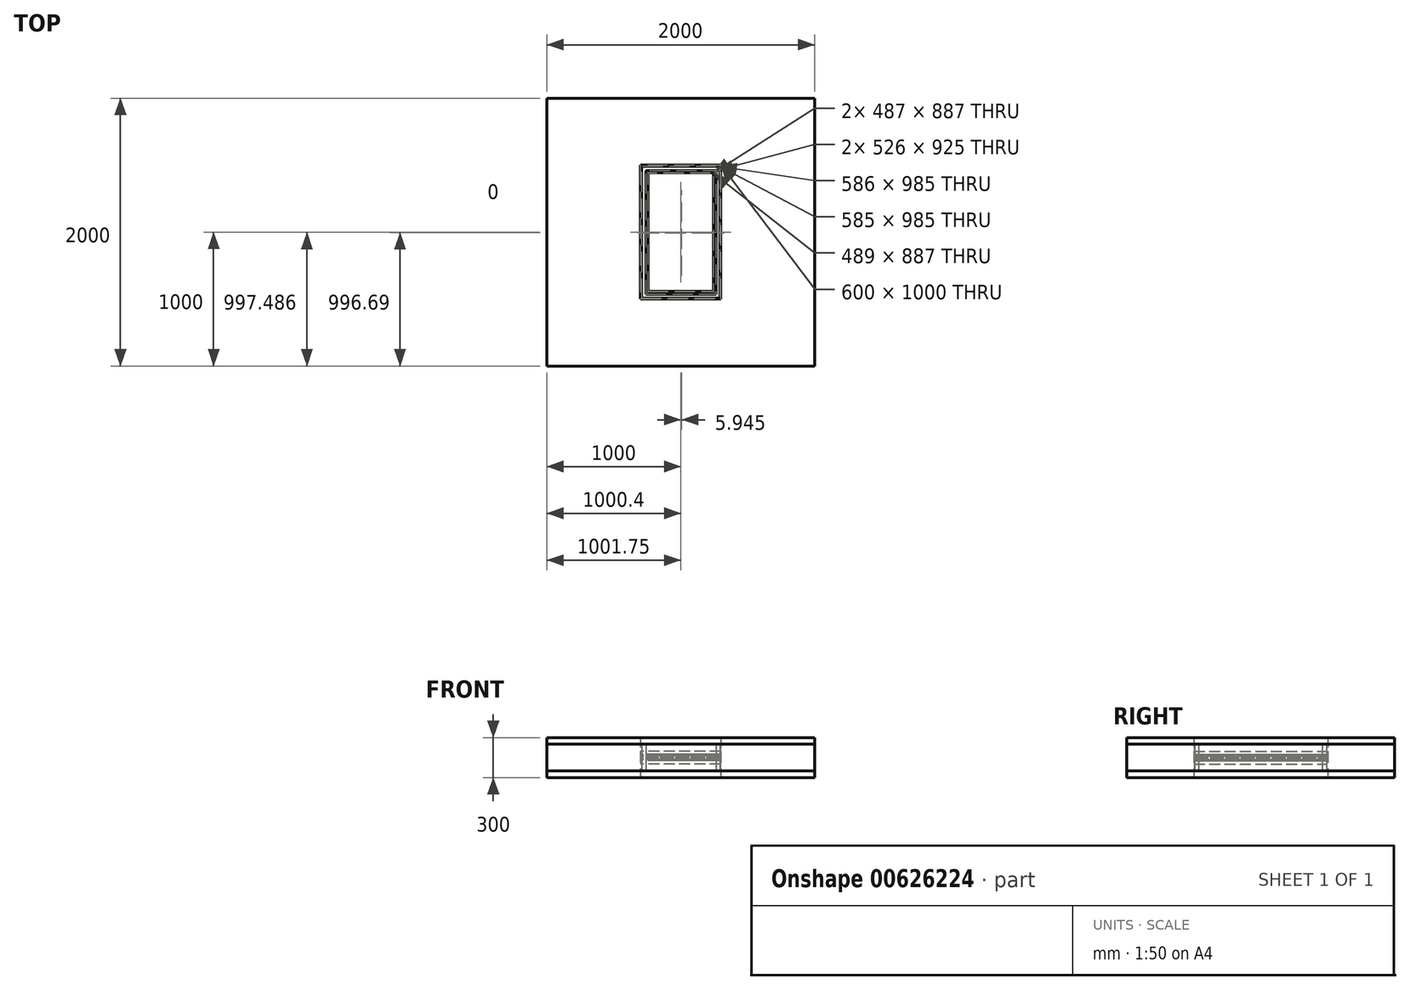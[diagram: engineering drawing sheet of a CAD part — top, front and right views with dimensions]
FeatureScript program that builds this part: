
annotation { "Feature Type Name" : "Feature", "Feature Type Description" : "" }
export const myFeature = defineFeature(function(context is Context, id is Id, definition is map)
    precondition{}
    {
        {
            var Q0;
            Q0=qCreatedBy(makeId("Top.planeOp"),FACE);
            var sketch = newSketch(context, id + "F0", { "sketchPlane" : qUnion([Q0])});
            skLineSegment(sketch, "E0.bottom", {"start": v(300, -500) * mm, "end": v(-300, -500) * mm});
            skLineSegment(sketch, "E0.top", {"start": v(300, 500) * mm, "end": v(-300, 500) * mm});
            skLineSegment(sketch, "E0.left", {"start": v(300, -500) * mm, "end": v(300, 500) * mm});
            skLineSegment(sketch, "E0.right", {"start": v(-300, -500) * mm, "end": v(-300, 500) * mm});
            skPoint(sketch, "E0.middle", {"position": v(0, 0) * mm});
            skLineSegment(sketch, "E1.0", {"start": v(-292.5, -492.5) * mm, "end": v(-292.5, 492.5) * mm});
            skLineSegment(sketch, "E1.1", {"start": v(292.5, -492.5) * mm, "end": v(-292.5, -492.5) * mm});
            skLineSegment(sketch, "E1.2", {"start": v(292.5, -492.5) * mm, "end": v(292.5, 492.5) * mm});
            skLineSegment(sketch, "E1.3", {"start": v(292.5, 492.5) * mm, "end": v(-292.5, 492.5) * mm});
            skSolve(sketch);
        }
        {
            var Q0;
            Q0 = qSketchRegion(id + "F0", true);
            extrude(context, id + "F1", {"entities" : qUnion([Q0]), "endBound" : BoundingType.SYMMETRIC, "depth" : 96 * mm, "offsetDistance" : 25 * mm});
        }
        {
            var Q0;
            Q0=qCreatedBy(makeId("Top.planeOp"),FACE);
            var sketch = newSketch(context, id + "F2", { "sketchPlane" : qUnion([Q0])});
            skPoint(sketch, "E2.middle", {"position": v(0, 0) * mm});
            skLineSegment(sketch, "E3.0", {"start": v(-292.5, -492.5) * mm, "end": v(-292.5, 492.5) * mm});
            skLineSegment(sketch, "E3.1", {"start": v(292.5, -492.5) * mm, "end": v(-292.5, -492.5) * mm});
            skLineSegment(sketch, "E3.2", {"start": v(292.5, -492.5) * mm, "end": v(292.5, 492.5) * mm});
            skLineSegment(sketch, "E3.3", {"start": v(292.5, 492.5) * mm, "end": v(-292.5, 492.5) * mm});
            skLineSegment(sketch, "E4.0", {"start": v(243.5, -443.5) * mm, "end": v(243.5, 443.5) * mm});
            skLineSegment(sketch, "E4.1", {"start": v(243.5, -443.5) * mm, "end": v(-243.5, -443.5) * mm});
            skLineSegment(sketch, "E4.2", {"start": v(-243.5, -443.5) * mm, "end": v(-243.5, 443.5) * mm});
            skLineSegment(sketch, "E4.3", {"start": v(243.5, 443.5) * mm, "end": v(-243.5, 443.5) * mm});
            skSolve(sketch);
        }
        {
            var Q0;
            Q0=makeQuery(id+"F2.imprint","IMPRINT",FACE,{"disambiguationData":[TD([[makeQuery(id+"F2.imprint","IMPRINT",EDGE,{"derivedFrom":sQuery(id+"F2.wireOp",EDGE,"E3.0")}),-1.0]])]});
            extrude(context, id + "F3", {"entities" : qUnion([Q0]), "endBound" : BoundingType.SYMMETRIC, "depth" : 48 * mm, "offsetDistance" : 25 * mm});
        }
        {
            var Q0;
            Q0=qCreatedBy(makeId("Top.planeOp"),FACE);
            var sketch = newSketch(context, id + "F4", { "sketchPlane" : qUnion([Q0])});
            skPoint(sketch, "E5.middle", {"position": v(5.95, -5.93) * mm});
            skLineSegment(sketch, "E6.0", {"start": v(-286.55, -498.43) * mm, "end": v(-286.55, 486.57) * mm});
            skLineSegment(sketch, "E6.1", {"start": v(298.45, -498.43) * mm, "end": v(-286.55, -498.43) * mm});
            skLineSegment(sketch, "E6.2", {"start": v(298.45, -498.43) * mm, "end": v(298.45, 486.57) * mm});
            skLineSegment(sketch, "E6.3", {"start": v(298.45, 486.57) * mm, "end": v(-286.55, 486.57) * mm});
            skLineSegment(sketch, "E7.0", {"start": v(249.45, -449.43) * mm, "end": v(249.45, 437.57) * mm});
            skLineSegment(sketch, "E7.1", {"start": v(249.45, -449.43) * mm, "end": v(-237.55, -449.43) * mm});
            skLineSegment(sketch, "E7.2", {"start": v(-237.55, -449.43) * mm, "end": v(-237.55, 437.57) * mm});
            skLineSegment(sketch, "E7.3", {"start": v(249.45, 437.57) * mm, "end": v(-237.55, 437.57) * mm});
            skSolve(sketch);
        }
        {
            var Q0;
            Q0=makeQuery(id+"F4.imprint","IMPRINT",FACE,{"disambiguationData":[TD([[makeQuery(id+"F4.imprint","IMPRINT",EDGE,{"derivedFrom":sQuery(id+"F4.wireOp",EDGE,"E6.0")}),-1.0]])]});
            extrude(context, id + "F5", {"entities" : qUnion([Q0]), "endBound" : BoundingType.SYMMETRIC, "depth" : 24 * mm, "offsetDistance" : 25 * mm});
        }
        {
            var Q0;
            Q0=qCreatedBy(makeId("Top.planeOp"),FACE);
            var sketch = newSketch(context, id + "F6", { "sketchPlane" : qUnion([Q0])});
            skLineSegment(sketch, "E8.0", {"start": v(-291.25, -495.01) * mm, "end": v(-291.25, 489.99) * mm});
            skLineSegment(sketch, "E8.1", {"start": v(294.75, -495.01) * mm, "end": v(-291.25, -495.01) * mm});
            skLineSegment(sketch, "E8.2", {"start": v(294.75, -495.01) * mm, "end": v(294.75, 489.99) * mm});
            skLineSegment(sketch, "E8.3", {"start": v(294.75, 489.99) * mm, "end": v(-291.25, 489.99) * mm});
            skLineSegment(sketch, "E9.0", {"start": v(264.75, 459.99) * mm, "end": v(-261.25, 459.99) * mm});
            skLineSegment(sketch, "E9.1", {"start": v(264.75, -465.01) * mm, "end": v(264.75, 459.99) * mm});
            skLineSegment(sketch, "E9.2", {"start": v(264.75, -465.01) * mm, "end": v(-261.25, -465.01) * mm});
            skLineSegment(sketch, "E9.3", {"start": v(-261.25, -465.01) * mm, "end": v(-261.25, 459.99) * mm});
            skSolve(sketch);
        }
        {
            var Q0;
            Q0=makeQuery(id+"F6.imprint","IMPRINT",FACE,{"disambiguationData":[TD([[makeQuery(id+"F6.imprint","IMPRINT",EDGE,{"derivedFrom":sQuery(id+"F6.wireOp",EDGE,"E9.0")}),1.0]])]});
            extrude(context, id + "F7", {"entities" : qUnion([Q0]), "depth" : 25 * mm, "offsetDistance" : 25 * mm});
        }
        {
            var Q0;
            Q0=makeQuery(id+"F7.opExtrude","SWEPT_BODY",BODY,{"disambiguationData":[OSD([sQuery(id+"F6.wireOp",EDGE,"E9.0"),sQuery(id+"F6.wireOp",EDGE,"E9.1"),sQuery(id+"F6.wireOp",EDGE,"E9.2"),sQuery(id+"F6.wireOp",EDGE,"E9.3")])]});
            deleteBodies(context, id + "F8", {"entities" : qUnion([Q0])});
        }
        {
            var Q0;
            Q0=makeQuery(id+"F6.imprint","IMPRINT",FACE,{"disambiguationData":[TD([[makeQuery(id+"F6.imprint","IMPRINT",EDGE,{"derivedFrom":sQuery(id+"F6.wireOp",EDGE,"E8.0")}),-1.0]])]});
            extrude(context, id + "F9", {"entities" : qUnion([Q0]), "depth" : 24 * mm, "offsetDistance" : 25 * mm});
        }
        {
            var Q0;
            Q0=makeQuery(id+"F6.imprint","IMPRINT",FACE,{"disambiguationData":[TD([[makeQuery(id+"F6.imprint","IMPRINT",EDGE,{"derivedFrom":sQuery(id+"F6.wireOp",EDGE,"E9.0")}),1.0]])]});
            var sketch = newSketch(context, id + "F10", { "sketchPlane" : qUnion([Q0])});
            skLineSegment(sketch, "E10.0", {"start": v(263.9, 459.2) * mm, "end": v(-263.1, 459.2) * mm});
            skLineSegment(sketch, "E10.1", {"start": v(263.9, -465.8) * mm, "end": v(263.9, 459.2) * mm});
            skLineSegment(sketch, "E10.2", {"start": v(263.9, -465.8) * mm, "end": v(-263.1, -465.8) * mm});
            skLineSegment(sketch, "E10.3", {"start": v(-263.1, -465.8) * mm, "end": v(-263.1, 459.2) * mm});
            skLineSegment(sketch, "E11.0", {"start": v(-244.1, -446.8) * mm, "end": v(-244.1, 440.2) * mm});
            skLineSegment(sketch, "E11.1", {"start": v(244.9, -446.8) * mm, "end": v(-244.1, -446.8) * mm});
            skLineSegment(sketch, "E11.2", {"start": v(244.9, -446.8) * mm, "end": v(244.9, 440.2) * mm});
            skLineSegment(sketch, "E11.3", {"start": v(244.9, 440.2) * mm, "end": v(-244.1, 440.2) * mm});
            skSolve(sketch);
        }
        {
            var Q0;
            Q0=makeQuery(id+"F10.imprint","IMPRINT",FACE,{"disambiguationData":[TD([[makeQuery(id+"F10.imprint","IMPRINT",EDGE,{"derivedFrom":sQuery(id+"F10.wireOp",EDGE,"E11.0")}),1.0]])]});
            extrude(context, id + "F11", {"entities" : qUnion([Q0]), "endBound" : BoundingType.SYMMETRIC, "depth" : 24 * mm, "offsetDistance" : 25 * mm});
        }
        {
            var Q0;
            Q0=makeQuery(id+"F6.imprint","IMPRINT",FACE,{"disambiguationData":[TD([[makeQuery(id+"F6.imprint","IMPRINT",EDGE,{"derivedFrom":sQuery(id+"F6.wireOp",EDGE,"E8.0")}),-1.0]])]});
            extrude(context, id + "F12", {"entities" : qUnion([Q0]), "endBound" : BoundingType.SYMMETRIC, "depth" : 200 * mm, "offsetDistance" : 25 * mm});
        }
        {
            var Q0;
            Q0=qCreatedBy(makeId("Top.planeOp"),FACE);
            var sketch = newSketch(context, id + "F13", { "sketchPlane" : qUnion([Q0])});
            skLineSegment(sketch, "E12.0", {"start": v(-293, -492.5) * mm, "end": v(-293, 492.5) * mm});
            skLineSegment(sketch, "E12.1", {"start": v(293, -492.5) * mm, "end": v(-293, -492.5) * mm});
            skLineSegment(sketch, "E12.2", {"start": v(293, -492.5) * mm, "end": v(293, 492.5) * mm});
            skLineSegment(sketch, "E12.3", {"start": v(293, 492.5) * mm, "end": v(-293, 492.5) * mm});
            skLineSegment(sketch, "E13.bottom", {"start": v(1000, -1000) * mm, "end": v(-1000, -1000) * mm});
            skLineSegment(sketch, "E13.top", {"start": v(1000, 1000) * mm, "end": v(-1000, 1000) * mm});
            skLineSegment(sketch, "E13.left", {"start": v(1000, -1000) * mm, "end": v(1000, 1000) * mm});
            skLineSegment(sketch, "E13.right", {"start": v(-1000, -1000) * mm, "end": v(-1000, 1000) * mm});
            skPoint(sketch, "E13.middle", {"position": v(0, 0) * mm});
            skSolve(sketch);
        }
        {
            var Q0;
            Q0=makeQuery(id+"F13.imprint","IMPRINT",FACE,{"disambiguationData":[TD([[makeQuery(id+"F13.imprint","IMPRINT",EDGE,{"derivedFrom":sQuery(id+"F13.wireOp",EDGE,"E12.0")}),1.0]])]});
            extrude(context, id + "F14", {"entities" : qUnion([Q0]), "endBound" : BoundingType.SYMMETRIC, "depth" : 200 * mm, "offsetDistance" : 25 * mm});
        }
        {
            var Q0;
            Q0=qCreatedBy(makeId("Top.planeOp"),FACE);
            var sketch = newSketch(context, id + "F15", { "sketchPlane" : qUnion([Q0])});
            skLineSegment(sketch, "E14.bottom", {"start": v(300, -500) * mm, "end": v(-300, -500) * mm});
            skLineSegment(sketch, "E14.top", {"start": v(300, 500) * mm, "end": v(-300, 500) * mm});
            skLineSegment(sketch, "E14.left", {"start": v(300, -500) * mm, "end": v(300, 500) * mm});
            skLineSegment(sketch, "E14.right", {"start": v(-300, -500) * mm, "end": v(-300, 500) * mm});
            skPoint(sketch, "E14.middle", {"position": v(0, 0) * mm});
            skLineSegment(sketch, "E15.bottom", {"start": v(1000, -1000) * mm, "end": v(-1000, -1000) * mm});
            skLineSegment(sketch, "E15.top", {"start": v(1000, 1000) * mm, "end": v(-1000, 1000) * mm});
            skLineSegment(sketch, "E15.left", {"start": v(1000, -1000) * mm, "end": v(1000, 1000) * mm});
            skLineSegment(sketch, "E15.right", {"start": v(-1000, -1000) * mm, "end": v(-1000, 1000) * mm});
            skSolve(sketch);
        }
        {
            var Q0;
            Q0=makeQuery(id+"F15.imprint","IMPRINT",FACE,{"disambiguationData":[TD([[makeQuery(id+"F15.imprint","IMPRINT",EDGE,{"derivedFrom":sQuery(id+"F15.wireOp",EDGE,"E14.bottom")}),1.0]])]});
            extrude(context, id + "F16", {"entities" : qUnion([Q0]), "endBound" : BoundingType.SYMMETRIC, "depth" : 300 * mm, "offsetDistance" : 25 * mm});
        }
        {
            var Q0;
            Q0=makeQuery(id+"F2.imprint","IMPRINT",FACE,{"disambiguationData":[TD([[makeQuery(id+"F2.imprint","IMPRINT",EDGE,{"derivedFrom":sQuery(id+"F2.wireOp",EDGE,"E4.0")}),1.0]])]});
            extrude(context, id + "F17", {"entities" : qUnion([Q0]), "endBound" : BoundingType.SYMMETRIC, "depth" : 48 * mm, "offsetDistance" : 25 * mm});
        }
    });
